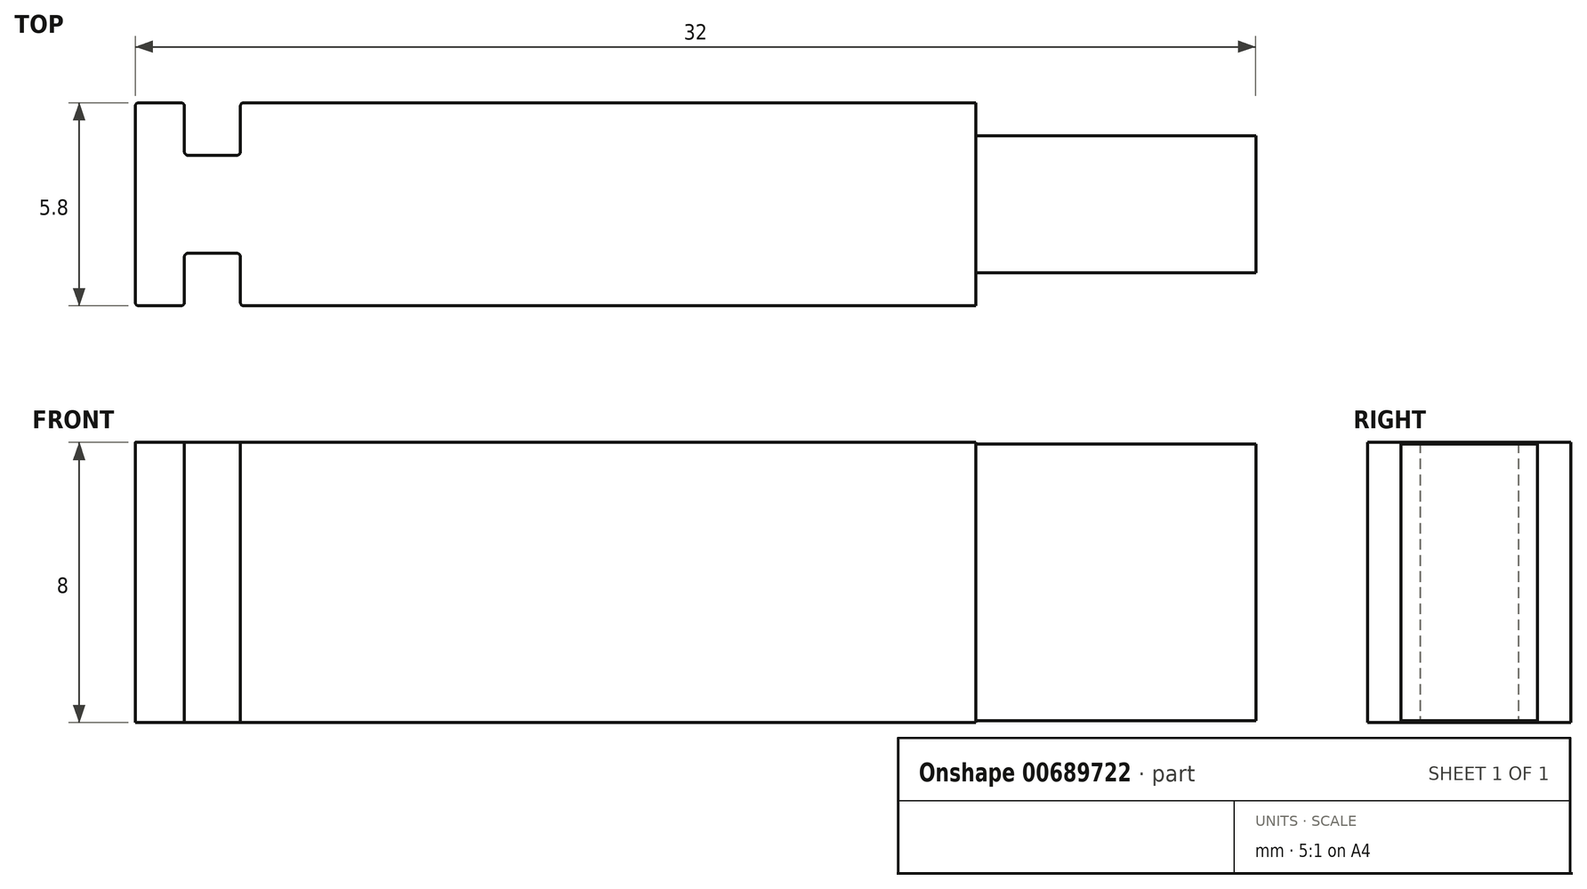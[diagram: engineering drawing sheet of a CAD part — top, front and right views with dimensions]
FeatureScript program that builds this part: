
annotation { "Feature Type Name" : "Feature", "Feature Type Description" : "" }
export const myFeature = defineFeature(function(context is Context, id is Id, definition is map)
    precondition{}
    {
        {
            var Q0;
            Q0=qCreatedBy(makeId("Top.planeOp"),FACE);
            var sketch = newSketch(context, id + "F0", { "sketchPlane" : qUnion([Q0])});
            skLineSegment(sketch, "E0.bottom", {"start": v(-45.17, 5.66) * mm, "end": v(-16.17, 5.66) * mm});
            skLineSegment(sketch, "E0.top", {"start": v(-45.17, -0.14) * mm, "end": v(-16.17, -0.14) * mm});
            skLineSegment(sketch, "E0.right", {"start": v(-16.17, 5.66) * mm, "end": v(-16.17, -0.14) * mm});
            skLineSegment(sketch, "E1", {"start": v(-45.17, 5.66) * mm, "end": v(-45.17, 4.16) * mm});
            skLineSegment(sketch, "E2", {"start": v(-45.17, 4.16) * mm, "end": v(-46.77, 4.16) * mm});
            skLineSegment(sketch, "E3", {"start": v(-46.77, 4.16) * mm, "end": v(-46.77, 5.66) * mm});
            skLineSegment(sketch, "E4", {"start": v(-43.67, 2.76) * mm, "end": v(-52.24, 2.76) * mm, "construction": true});
            skLineSegment(sketch, "E5.MirrorCS", {"start": v(-46.77, -0.14) * mm, "end": v(-48.17, -0.14) * mm});
            skLineSegment(sketch, "E6.MirrorCS", {"start": v(-46.77, 1.36) * mm, "end": v(-46.77, -0.14) * mm});
            skLineSegment(sketch, "E7.MirrorCS", {"start": v(-45.17, 1.36) * mm, "end": v(-46.77, 1.36) * mm});
            skLineSegment(sketch, "E8.MirrorCS", {"start": v(-45.17, -0.14) * mm, "end": v(-45.17, 1.36) * mm});
            skLineSegment(sketch, "E9", {"start": v(-48.17, 5.66) * mm, "end": v(-48.17, -0.14) * mm});
            skLineSegment(sketch, "E10", {"start": v(-48.17, 5.66) * mm, "end": v(-46.77, 5.66) * mm});
            skSolve(sketch);
        }
        {
            var Q0;
            Q0=makeQuery(id+"F0.imprint","IMPRINT",FACE,{"disambiguationData":[TD([[makeQuery(id+"F0.imprint","IMPRINT",EDGE,{"derivedFrom":sQuery(id+"F0.wireOp",EDGE,"E0.bottom")}),-1.0]])]});
            var Q1;
            Q1=makeQuery(id+"F0.imprint","IMPRINT",FACE,{"disambiguationData":[TD([[makeQuery(id+"F0.imprint","IMPRINT",EDGE,{"derivedFrom":sQuery(id+"F0.wireOp",EDGE,"E0.right")}),1.0]])]});
            extrude(context, id + "F1", {"entities" : qUnion([Q0, Q1]), "depth" : 8 * mm, "offsetDistance" : 25 * mm});
        }
        {
            var Q0;
            Q0=makeQuery(id+"F1.opExtrude","SWEPT_FACE",FACE,{"disambiguationData":[OSD([sQuery(id+"F0.wireOp",EDGE,"E0.right")])]});
            var sketch = newSketch(context, id + "F2", { "sketchPlane" : qUnion([Q0])});
            skLineSegment(sketch, "E11.left", {"start": v(2.76, 8) * mm, "end": v(2.76, 0) * mm, "construction": true});
            skLineSegment(sketch, "E12", {"start": v(2.76, 0.05) * mm, "end": v(0.8, 0.05) * mm});
            skLineSegment(sketch, "E13", {"start": v(-0.14, 4) * mm, "end": v(5.66, 4) * mm, "construction": true});
            skLineSegment(sketch, "E14", {"start": v(0.8, 0.05) * mm, "end": v(0.8, 4) * mm});
            skLineSegment(sketch, "E15.MirrorCS", {"start": v(0.8, 7.95) * mm, "end": v(0.8, 4) * mm});
            skLineSegment(sketch, "E16.MirrorCS", {"start": v(2.76, 7.95) * mm, "end": v(0.8, 7.95) * mm});
            skLineSegment(sketch, "E17.MirrorCS", {"start": v(4.7, 0.05) * mm, "end": v(4.7, 4) * mm});
            skLineSegment(sketch, "E18.MirrorCS", {"start": v(2.76, 0.05) * mm, "end": v(4.7, 0.05) * mm});
            skLineSegment(sketch, "E19.MirrorCS", {"start": v(4.7, 7.95) * mm, "end": v(4.7, 4) * mm});
            skLineSegment(sketch, "E20.MirrorCS", {"start": v(2.76, 7.95) * mm, "end": v(4.7, 7.95) * mm});
            skSolve(sketch);
        }
        {
            var Q0;
            {var subQ0=sQuery(id+"F2.wireOp",EDGE,"E11.left");Q0=makeQuery(id+"F2.imprint","IMPRINT",FACE,{"disambiguationData":[TD([[makeQuery(id+"F2.imprint","IMPRINT",EDGE,{"derivedFrom":subQ0}),-1.0]])]});}
            var Q1;
            {var subQ0=sQuery(id+"F2.wireOp",EDGE,"E11.right");Q1=makeQuery(id+"F2.imprint","IMPRINT",FACE,{"disambiguationData":[TD([[makeQuery(id+"F2.imprint","IMPRINT",EDGE,{"derivedFrom":subQ0}),1.0]])]});}
            var Q2;
            Q2=makeQuery(id+"F2.imprint","IMPRINT",FACE,{"disambiguationData":[TD([[makeQuery(id+"F2.imprint","IMPRINT",EDGE,{"derivedFrom":sQuery(id+"F2.wireOp",EDGE,"E12")}),1.0]])]});
            extrude(context, id + "F3", {"entities" : qUnion([Q0, Q1, Q2]), "operationType" : NewBodyOperationType.REMOVE, "oppositeDirection" : true, "depth" : 8 * mm, "offsetDistance" : 25 * mm});
        }
        {
            var Q0;
            Q0=makeQuery(id+"F1.opExtrude","SWEPT_EDGE",EDGE,{"disambiguationData":[OSD([sQuery(id+"F0.wireOp",EDGE,"E5.MirrorCS"),sQuery(id+"F0.wireOp",EDGE,"E6.MirrorCS")])]});
            var Q1;
            Q1=makeQuery(id+"F1.opExtrude","SWEPT_EDGE",EDGE,{"disambiguationData":[OSD([sQuery(id+"F0.wireOp",EDGE,"E6.MirrorCS"),sQuery(id+"F0.wireOp",EDGE,"E7.MirrorCS")])]});
            var Q2;
            Q2=makeQuery(id+"F1.opExtrude","SWEPT_EDGE",EDGE,{"disambiguationData":[OSD([sQuery(id+"F0.wireOp",EDGE,"E2"),sQuery(id+"F0.wireOp",EDGE,"E3")])]});
            var Q3;
            Q3=makeQuery(id+"F1.opExtrude","SWEPT_EDGE",EDGE,{"disambiguationData":[OSD([sQuery(id+"F0.wireOp",EDGE,"E3"),sQuery(id+"F0.wireOp",EDGE,"E10")])]});
            var Q4;
            Q4=makeQuery(id+"F1.opExtrude","SWEPT_EDGE",EDGE,{"disambiguationData":[OSD([sQuery(id+"F0.wireOp",EDGE,"E9"),sQuery(id+"F0.wireOp",EDGE,"E10")])]});
            var Q5;
            Q5=makeQuery(id+"F1.opExtrude","SWEPT_EDGE",EDGE,{"disambiguationData":[OSD([sQuery(id+"F0.wireOp",EDGE,"E5.MirrorCS"),sQuery(id+"F0.wireOp",EDGE,"E9")])]});
            var Q6;
            Q6=makeQuery(id+"F1.opExtrude","SWEPT_EDGE",EDGE,{"disambiguationData":[OSD([sQuery(id+"F0.wireOp",EDGE,"E0.top"),sQuery(id+"F0.wireOp",EDGE,"E8.MirrorCS")])]});
            var Q7;
            Q7=makeQuery(id+"F1.opExtrude","SWEPT_EDGE",EDGE,{"disambiguationData":[OSD([sQuery(id+"F0.wireOp",EDGE,"E0.bottom"),sQuery(id+"F0.wireOp",EDGE,"E1")])]});
            var Q8;
            Q8=makeQuery(id+"F1.opExtrude","SWEPT_EDGE",EDGE,{"disambiguationData":[OSD([sQuery(id+"F0.wireOp",EDGE,"E1"),sQuery(id+"F0.wireOp",EDGE,"E2")])]});
            var Q9;
            Q9=makeQuery(id+"F1.opExtrude","SWEPT_EDGE",EDGE,{"disambiguationData":[OSD([sQuery(id+"F0.wireOp",EDGE,"E7.MirrorCS"),sQuery(id+"F0.wireOp",EDGE,"E8.MirrorCS")])]});
            fillet(context, id + "F4", {"entities" : qUnion([Q0, Q1, Q2, Q3, Q4, Q5, Q6, Q7, Q8, Q9]), "radius" : .1 * mm, "tangentPropagation" : true, "allowEdgeOverflow" : false});
        }
    });
